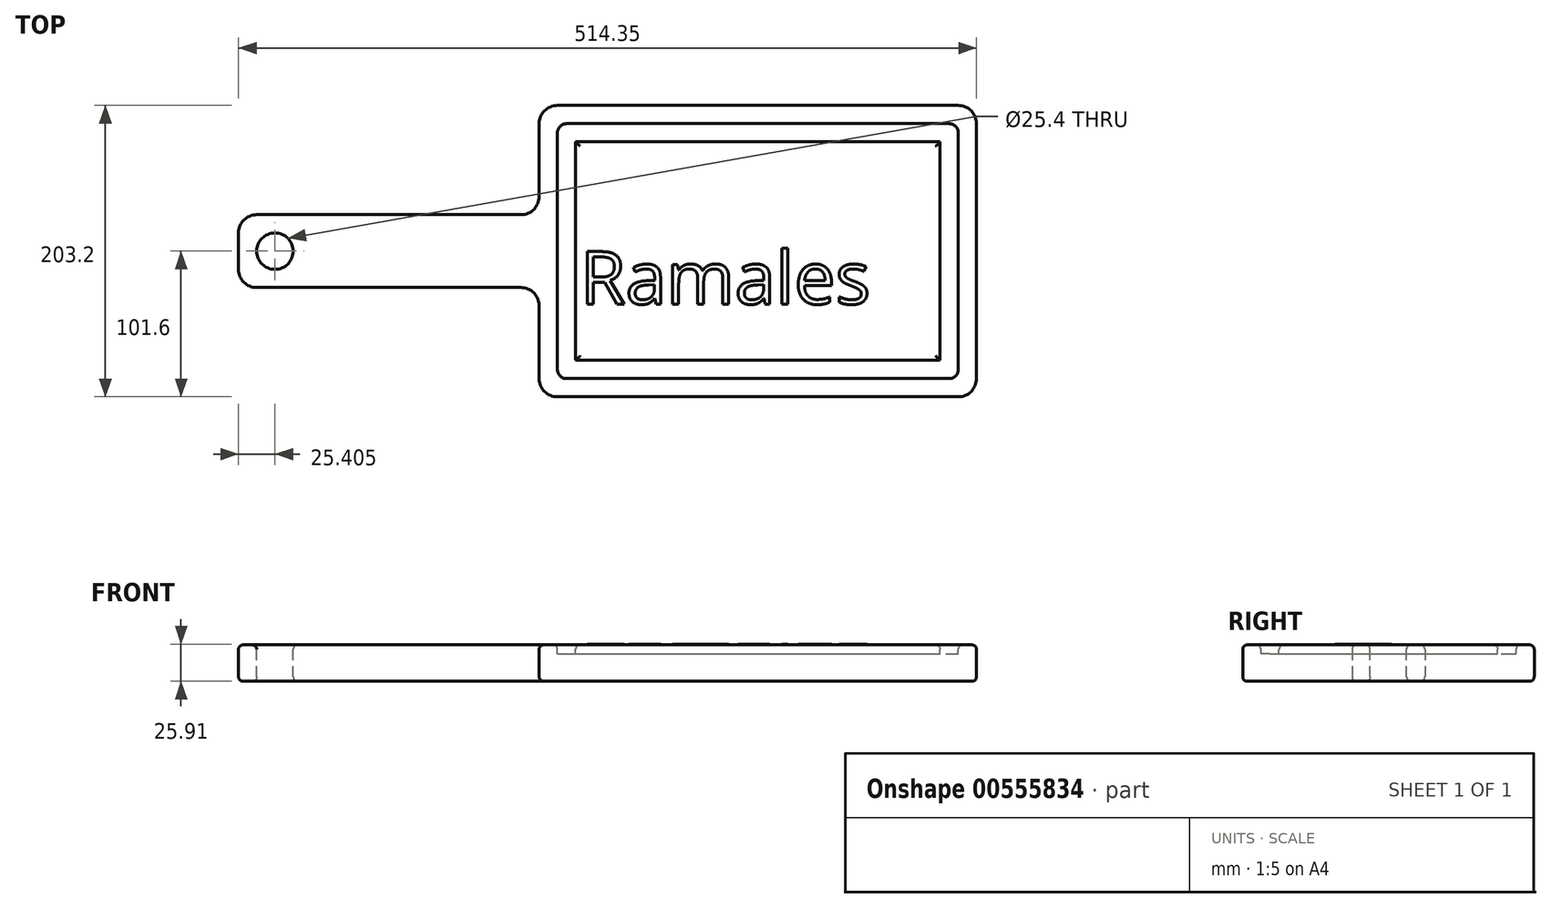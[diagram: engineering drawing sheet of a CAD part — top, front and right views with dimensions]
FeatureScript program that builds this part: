
annotation { "Feature Type Name" : "Feature", "Feature Type Description" : "" }
export const myFeature = defineFeature(function(context is Context, id is Id, definition is map)
    precondition{}
    {
        {
            var Q0;
            Q0=qCreatedBy(makeId("Top.planeOp"),FACE);
            var sketch = newSketch(context, id + "F0", { "sketchPlane" : qUnion([Q0])});
            skLineSegment(sketch, "E0.bottom", {"start": v(0, 0) * mm, "end": v(304.8, 0) * mm});
            skLineSegment(sketch, "E0.top", {"start": v(0, 203.2) * mm, "end": v(304.8, 203.2) * mm});
            skLineSegment(sketch, "E0.left", {"start": v(0, 0) * mm, "end": v(0, 76.2) * mm});
            skLineSegment(sketch, "E0.right", {"start": v(304.8, 0) * mm, "end": v(304.8, 203.2) * mm});
            skLineSegment(sketch, "E1.bottom", {"start": v(0, 127) * mm, "end": v(-209.55, 127) * mm});
            skLineSegment(sketch, "E1.top", {"start": v(0, 76.2) * mm, "end": v(-209.55, 76.2) * mm});
            skLineSegment(sketch, "E1.right", {"start": v(-209.55, 127) * mm, "end": v(-209.55, 76.2) * mm});
            skLineSegment(sketch, "E2.trimOffspring", {"start": v(0, 127) * mm, "end": v(0, 203.2) * mm});
            skSolve(sketch);
        }
        {
            var Q0;
            Q0=makeQuery(id+"F0.imprint","IMPRINT",FACE,{"disambiguationData":[TD([[makeQuery(id+"F0.imprint","IMPRINT",EDGE,{"derivedFrom":sQuery(id+"F0.wireOp",EDGE,"E0.bottom")}),1.0]])]});
            extrude(context, id + "F1", {"entities" : qUnion([Q0]), "depth" : 25.4 * mm, "offsetDistance" : 25.4 * mm});
        }
        {
            var Q0;
            Q0=makeQuery(id+"F1.opExtrude","CAP_FACE",FACE,{"disambiguationData":[OSD([sQuery(id+"F0.wireOp",EDGE,"E0.bottom"),sQuery(id+"F0.wireOp",EDGE,"E0.top"),sQuery(id+"F0.wireOp",EDGE,"E0.left"),sQuery(id+"F0.wireOp",EDGE,"E0.right"),sQuery(id+"F0.wireOp",EDGE,"E1.bottom"),sQuery(id+"F0.wireOp",EDGE,"E1.top"),sQuery(id+"F0.wireOp",EDGE,"E1.right"),sQuery(id+"F0.wireOp",EDGE,"E2.trimOffspring")])],"isStart":false});
            var sketch = newSketch(context, id + "F2", { "sketchPlane" : qUnion([Q0])});
            skCircle(sketch, "E3", {"center": v(-184.15, 101.6) * mm, "radius": 12.7 * mm});
            skSolve(sketch);
        }
        {
            var Q0;
            Q0 = qSketchRegion(id + "F2", true);
            extrude(context, id + "F3", {"entities" : qUnion([Q0]), "operationType" : NewBodyOperationType.REMOVE, "oppositeDirection" : true, "depth" : 25.4 * mm, "offsetDistance" : 25.4 * mm});
        }
        {
            var Q0;
            Q0=makeQuery(id+"F1.opExtrude","CAP_FACE",FACE,{"disambiguationData":[OSD([sQuery(id+"F0.wireOp",EDGE,"E0.bottom"),sQuery(id+"F0.wireOp",EDGE,"E0.top"),sQuery(id+"F0.wireOp",EDGE,"E0.left"),sQuery(id+"F0.wireOp",EDGE,"E0.right"),sQuery(id+"F0.wireOp",EDGE,"E1.bottom"),sQuery(id+"F0.wireOp",EDGE,"E1.top"),sQuery(id+"F0.wireOp",EDGE,"E1.right"),sQuery(id+"F0.wireOp",EDGE,"E2.trimOffspring")])],"isStart":false});
            var sketch = newSketch(context, id + "F4", { "sketchPlane" : qUnion([Q0])});
            skLineSegment(sketch, "E4.5", {"start": v(-196.85, 114.3) * mm, "end": v(-196.85, 88.9) * mm});
            skLineSegment(sketch, "E5.0", {"start": v(12.7, 12.7) * mm, "end": v(12.7, 76.2) * mm});
            skLineSegment(sketch, "E5.1", {"start": v(12.7, 127) * mm, "end": v(12.7, 190.5) * mm});
            skLineSegment(sketch, "E5.2", {"start": v(12.7, 190.5) * mm, "end": v(292.1, 190.5) * mm});
            skLineSegment(sketch, "E5.3", {"start": v(292.1, 12.7) * mm, "end": v(292.1, 190.5) * mm});
            skLineSegment(sketch, "E5.4", {"start": v(12.7, 12.7) * mm, "end": v(292.1, 12.7) * mm});
            skLineSegment(sketch, "E6", {"start": v(12.7, 127) * mm, "end": v(12.7, 76.2) * mm});
            skLineSegment(sketch, "E7.0", {"start": v(25.4, 127) * mm, "end": v(25.4, 177.8) * mm});
            skLineSegment(sketch, "E7.1", {"start": v(279.4, 25.4) * mm, "end": v(279.4, 177.8) * mm});
            skLineSegment(sketch, "E7.2", {"start": v(25.4, 25.4) * mm, "end": v(279.4, 25.4) * mm});
            skLineSegment(sketch, "E7.3", {"start": v(25.4, 177.8) * mm, "end": v(279.4, 177.8) * mm});
            skLineSegment(sketch, "E7.4", {"start": v(25.4, 25.4) * mm, "end": v(25.4, 76.2) * mm});
            skLineSegment(sketch, "E7.5", {"start": v(25.4, 127) * mm, "end": v(25.4, 76.2) * mm});
            skSolve(sketch);
        }
        {
            var Q0;
            Q0=makeQuery(id+"F4.imprint","IMPRINT",FACE,{"disambiguationData":[TD([[makeQuery(id+"F4.imprint","IMPRINT",EDGE,{"derivedFrom":sQuery(id+"F4.wireOp",EDGE,"E5.0")}),-1.0]])]});
            extrude(context, id + "F5", {"entities" : qUnion([Q0]), "operationType" : NewBodyOperationType.REMOVE, "oppositeDirection" : true, "depth" : 6.35 * mm, "offsetDistance" : 25.4 * mm});
        }
        {
            var Q0;
            Q0=makeQuery(id+"F5.boolean.opBoolean","COPY",EDGE,{"derivedFrom":makeQuery(id+"F5.opExtrude","SWEPT_EDGE",EDGE,{"disambiguationData":[OSD([sQuery(id+"F4.wireOp",EDGE,"E5.1"),sQuery(id+"F4.wireOp",EDGE,"E5.2")])]})});
            var Q1;
            Q1=makeQuery(id+"F5.boolean.opBoolean","COPY",EDGE,{"derivedFrom":makeQuery(id+"F5.opExtrude","SWEPT_EDGE",EDGE,{"disambiguationData":[OSD([sQuery(id+"F4.wireOp",EDGE,"E5.2"),sQuery(id+"F4.wireOp",EDGE,"E5.3")])]})});
            var Q2;
            Q2=makeQuery(id+"F5.boolean.opBoolean","COPY",EDGE,{"derivedFrom":makeQuery(id+"F5.opExtrude","SWEPT_EDGE",EDGE,{"disambiguationData":[OSD([sQuery(id+"F4.wireOp",EDGE,"E5.3"),sQuery(id+"F4.wireOp",EDGE,"E5.4")])]})});
            var Q3;
            Q3=makeQuery(id+"F5.boolean.opBoolean","COPY",EDGE,{"derivedFrom":makeQuery(id+"F5.opExtrude","SWEPT_EDGE",EDGE,{"disambiguationData":[OSD([sQuery(id+"F4.wireOp",EDGE,"E5.0"),sQuery(id+"F4.wireOp",EDGE,"E5.4")])]})});
            fillet(context, id + "F6", {"entities" : qUnion([Q0, Q1, Q2, Q3]), "radius" : 6.35 * mm, "tangentPropagation" : true, "allowEdgeOverflow" : false});
        }
        {
            var Q0;
            Q0=makeQuery(id+"F1.opExtrude","SWEPT_EDGE",EDGE,{"disambiguationData":[OSD([sQuery(id+"F0.wireOp",EDGE,"E0.bottom"),sQuery(id+"F0.wireOp",EDGE,"E0.left")])]});
            var Q1;
            Q1=makeQuery(id+"F1.opExtrude","SWEPT_EDGE",EDGE,{"disambiguationData":[OSD([sQuery(id+"F0.wireOp",EDGE,"E1.top"),sQuery(id+"F0.wireOp",EDGE,"E1.right")])]});
            var Q2;
            Q2=makeQuery(id+"F1.opExtrude","SWEPT_EDGE",EDGE,{"disambiguationData":[OSD([sQuery(id+"F0.wireOp",EDGE,"E1.bottom"),sQuery(id+"F0.wireOp",EDGE,"E2.trimOffspring")])]});
            var Q3;
            Q3=makeQuery(id+"F1.opExtrude","SWEPT_EDGE",EDGE,{"disambiguationData":[OSD([sQuery(id+"F0.wireOp",EDGE,"E0.left"),sQuery(id+"F0.wireOp",EDGE,"E1.top")])]});
            var Q4;
            Q4=makeQuery(id+"F1.opExtrude","SWEPT_EDGE",EDGE,{"disambiguationData":[OSD([sQuery(id+"F0.wireOp",EDGE,"E1.bottom"),sQuery(id+"F0.wireOp",EDGE,"E1.right")])]});
            var Q5;
            Q5=makeQuery(id+"F1.opExtrude","SWEPT_EDGE",EDGE,{"disambiguationData":[OSD([sQuery(id+"F0.wireOp",EDGE,"E0.top"),sQuery(id+"F0.wireOp",EDGE,"E2.trimOffspring")])]});
            var Q6;
            Q6=makeQuery(id+"F1.opExtrude","SWEPT_EDGE",EDGE,{"disambiguationData":[OSD([sQuery(id+"F0.wireOp",EDGE,"E0.top"),sQuery(id+"F0.wireOp",EDGE,"E0.right")])]});
            var Q7;
            Q7=makeQuery(id+"F1.opExtrude","SWEPT_EDGE",EDGE,{"disambiguationData":[OSD([sQuery(id+"F0.wireOp",EDGE,"E0.bottom"),sQuery(id+"F0.wireOp",EDGE,"E0.right")])]});
            fillet(context, id + "F7", {"entities" : qUnion([Q0, Q1, Q2, Q3, Q4, Q5, Q6, Q7]), "radius" : 12.7 * mm, "tangentPropagation" : true, "allowEdgeOverflow" : false});
        }
        {
            var Q0;
            Q0=makeQuery(id+"F5.boolean.opBoolean","SPLIT",FACE,{"disambiguationData":[TD([makeQuery(id+"F5.opExtrude","SWEPT_FACE",FACE,{"disambiguationData":[OSD([sQuery(id+"F4.wireOp",EDGE,"E7.1")])]})])],"derivedFrom":makeQuery(id+"F1.opExtrude","CAP_FACE",FACE,{"disambiguationData":[OSD([sQuery(id+"F0.wireOp",EDGE,"E0.bottom"),sQuery(id+"F0.wireOp",EDGE,"E0.top"),sQuery(id+"F0.wireOp",EDGE,"E0.left"),sQuery(id+"F0.wireOp",EDGE,"E0.right"),sQuery(id+"F0.wireOp",EDGE,"E1.bottom"),sQuery(id+"F0.wireOp",EDGE,"E1.top"),sQuery(id+"F0.wireOp",EDGE,"E1.right"),sQuery(id+"F0.wireOp",EDGE,"E2.trimOffspring")])],"isStart":false})});
            var Q1;
            {var subQ0=sQuery(id+"F0.wireOp",EDGE,"E2.trimOffspring");var subQ1=sQuery(id+"F0.wireOp",EDGE,"E1.right");var subQ2=sQuery(id+"F0.wireOp",EDGE,"E1.top");var subQ3=sQuery(id+"F0.wireOp",EDGE,"E1.bottom");var subQ4=sQuery(id+"F0.wireOp",EDGE,"E0.bottom");var subQ5=sQuery(id+"F0.wireOp",EDGE,"E0.right");var subQ6=sQuery(id+"F0.wireOp",EDGE,"E0.top");var subQ7=sQuery(id+"F0.wireOp",EDGE,"E0.left");Q1=makeQuery(id+"F5.boolean.opBoolean","SPLIT",FACE,{"disambiguationData":[TD([makeQuery(id+"F1.opExtrude","SWEPT_FACE",FACE,{"disambiguationData":[OSD([subQ4])]})])],"derivedFrom":makeQuery(id+"F1.opExtrude","CAP_FACE",FACE,{"disambiguationData":[OSD([subQ4,subQ6,subQ7,subQ5,subQ3,subQ2,subQ1,subQ0])],"isStart":false})});}
            var Q2;
            Q2=makeQuery(id+"F1.opExtrude","CAP_FACE",FACE,{"disambiguationData":[OSD([sQuery(id+"F0.wireOp",EDGE,"E0.bottom"),sQuery(id+"F0.wireOp",EDGE,"E0.top"),sQuery(id+"F0.wireOp",EDGE,"E0.left"),sQuery(id+"F0.wireOp",EDGE,"E0.right"),sQuery(id+"F0.wireOp",EDGE,"E1.bottom"),sQuery(id+"F0.wireOp",EDGE,"E1.top"),sQuery(id+"F0.wireOp",EDGE,"E1.right"),sQuery(id+"F0.wireOp",EDGE,"E2.trimOffspring")])],"isStart":true});
            fillet(context, id + "F8", {"entities" : qUnion([Q0, Q1, Q2]), "radius" : 3.17 * mm, "tangentPropagation" : true, "allowEdgeOverflow" : false});
        }
        {
            var Q0;
            Q0=makeQuery(id+"F5.boolean.opBoolean","SPLIT",FACE,{"disambiguationData":[TD([makeQuery(id+"F5.opExtrude","SWEPT_FACE",FACE,{"disambiguationData":[OSD([sQuery(id+"F4.wireOp",EDGE,"E7.1")])]})])],"derivedFrom":makeQuery(id+"F1.opExtrude","CAP_FACE",FACE,{"disambiguationData":[OSD([sQuery(id+"F0.wireOp",EDGE,"E0.bottom"),sQuery(id+"F0.wireOp",EDGE,"E0.top"),sQuery(id+"F0.wireOp",EDGE,"E0.left"),sQuery(id+"F0.wireOp",EDGE,"E0.right"),sQuery(id+"F0.wireOp",EDGE,"E1.bottom"),sQuery(id+"F0.wireOp",EDGE,"E1.top"),sQuery(id+"F0.wireOp",EDGE,"E1.right"),sQuery(id+"F0.wireOp",EDGE,"E2.trimOffspring")])],"isStart":false})});
            var sketch = newSketch(context, id + "F9", { "sketchPlane" : qUnion([Q0])});
            skText(sketch, "E8", { "text": "Ramales", "fontName": "OpenSans-Regular.ttf"});
            const initialGuessF9  = {"E8": [0.02858, 0.06475, 1, 0, 0.03685]};
            skSetInitialGuess(sketch, initialGuessF9);
            skSolve(sketch);
        }
        {
            var Q0;
            Q0 = qSketchRegion(id + "F9", true);
            extrude(context, id + "F10", {"entities" : qUnion([Q0]), "operationType" : NewBodyOperationType.ADD, "depth" : 0.5 * mm, "offsetDistance" : 25.4 * mm});
        }
    });
